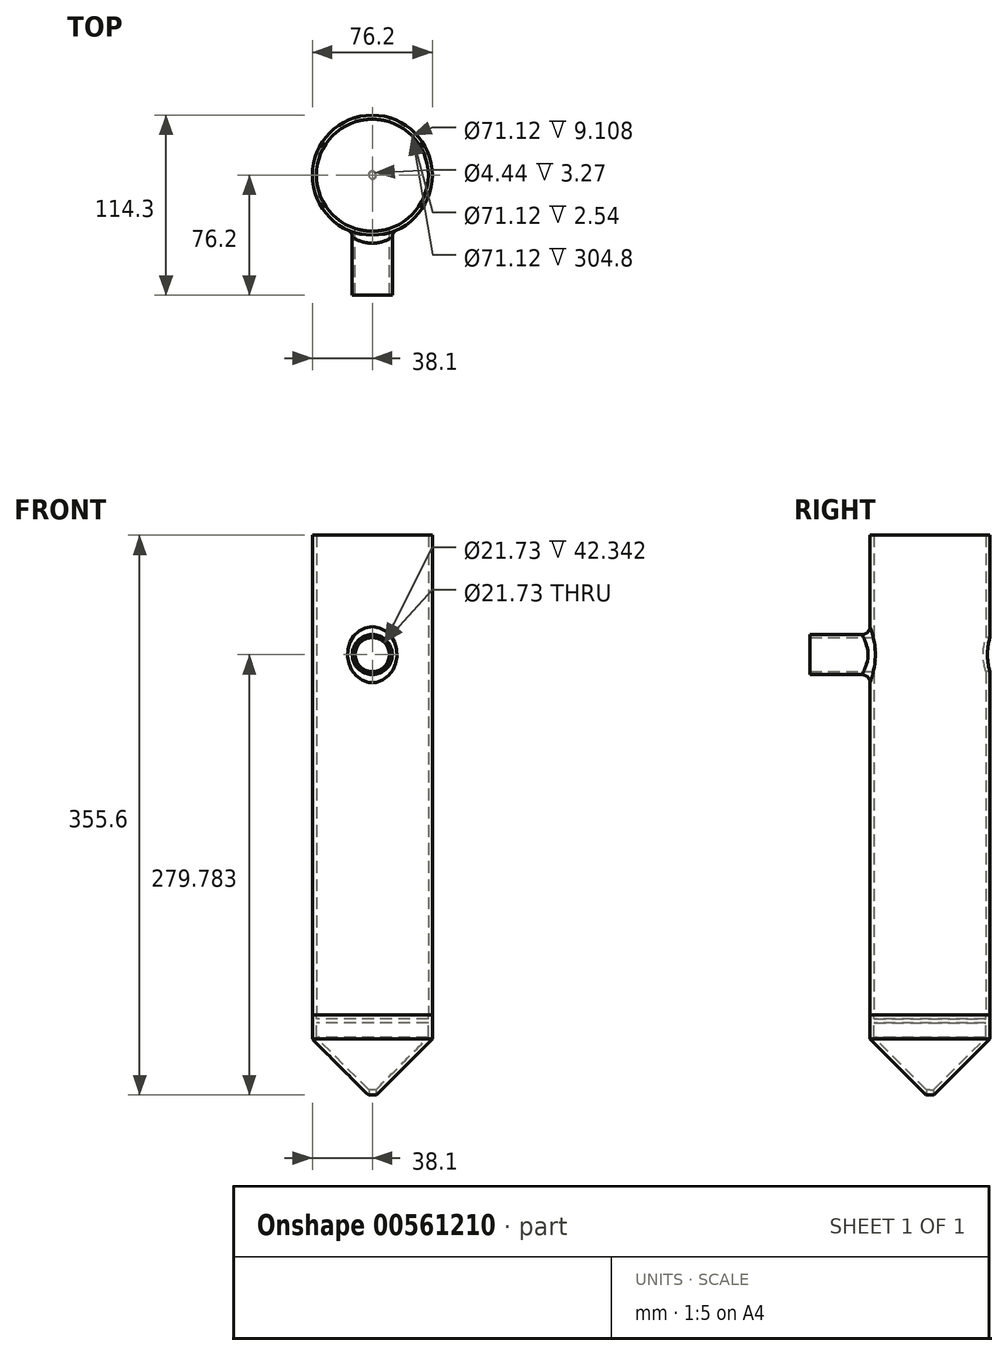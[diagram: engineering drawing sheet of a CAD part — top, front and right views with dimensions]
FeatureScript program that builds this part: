
annotation { "Feature Type Name" : "Feature", "Feature Type Description" : "" }
export const myFeature = defineFeature(function(context is Context, id is Id, definition is map)
    precondition{}
    {
        {
            var Q0;
            Q0=qCreatedBy(makeId("Top.planeOp"),FACE);
            var sketch = newSketch(context, id + "F0", { "sketchPlane" : qUnion([Q0])});
            skCircle(sketch, "E0", {"center": v(0, 0) * mm, "radius": 38.1 * mm});
            skSolve(sketch);
        }
        {
            var Q0;
            Q0 = qSketchRegion(id + "F0", true);
            extrude(context, id + "F1", {"entities" : qUnion([Q0]), "depth" : 304.8 * mm, "offsetDistance" : 25.4 * mm});
        }
        {
            var Q0;
            Q0=makeQuery(id+"F1.opExtrude","CAP_FACE",FACE,{"disambiguationData":[OSD([sQuery(id+"F0.wireOp",EDGE,"E0")])],"isStart":true});
            var sketch = newSketch(context, id + "F2", { "sketchPlane" : qUnion([Q0])});
            skCircle(sketch, "E1", {"center": v(0, 0) * mm, "radius": 38.1 * mm});
            skPoint(sketch, "E1.first.point", {"position": v(-6.24, 37.59) * mm});
            skPoint(sketch, "E1.second.point", {"position": v(37.6, -6.13) * mm});
            skPoint(sketch, "E1.third.point", {"position": v(-28.32, -25.5) * mm});
            skSolve(sketch);
        }
        {
            var Q0;
            Q0 = qSketchRegion(id + "F2", true);
            extrude(context, id + "F3", {"entities" : qUnion([Q0]), "depth" : 50.8 * mm, "offsetDistance" : 25.4 * mm});
        }
        {
            var Q0;
            Q0=makeQuery(id+"F3.opExtrude","CAP_EDGE",EDGE,{"disambiguationData":[OSD([sQuery(id+"F2.wireOp",EDGE,"E1")])],"isStart":false});
            chamfer(context, id + "F4", {"entities" : qUnion([Q0]), "width" : 35.56 * mm, "tangentPropagation" : true});
        }
        {
            var Q0;
            Q0=qCreatedBy(makeId("Front.planeOp"),FACE);
            var sketch = newSketch(context, id + "F5", { "sketchPlane" : qUnion([Q0])});
            skCircle(sketch, "E2", {"center": v(0, 228.98) * mm, "radius": 12.7 * mm});
            skCircle(sketch, "E3", {"center": v(0, 228.98) * mm, "radius": 10.87 * mm});
            skSolve(sketch);
        }
        {
            var Q0;
            Q0=makeQuery(id+"F1.opExtrude","CAP_FACE",FACE,{"disambiguationData":[OSD([sQuery(id+"F0.wireOp",EDGE,"E0")])],"isStart":false});
            shell(context, id + "F6", {"entities" : qUnion([Q0]), "thickness" : 2.54 * mm});
        }
        {
            var Q0;
            {var subQ0=sQuery(id+"F0.wireOp",EDGE,"E0");Q0=makeQuery(id+"F6.opShell","OFFSET_FACE",FACE,{"disambiguationData":[OSD([subQ0]),TDD([makeQuery(id+"F1.opExtrude","CAP_FACE",FACE,{"disambiguationData":[OSD([subQ0])],"isStart":true})])]});}
            var sketch = newSketch(context, id + "F7", { "sketchPlane" : qUnion([Q0])});
            skCircle(sketch, "E4", {"center": v(0, 0) * mm, "radius": 35.56 * mm});
            skPoint(sketch, "E4.first.point", {"position": v(-25.89, 24.38) * mm});
            skPoint(sketch, "E4.second.point", {"position": v(32.46, -14.53) * mm});
            skPoint(sketch, "E4.third.point", {"position": v(-23.4, -26.77) * mm});
            skSolve(sketch);
        }
        {
            var Q0;
            Q0 = qSketchRegion(id + "F7", true);
            extrude(context, id + "F8", {"entities" : qUnion([Q0]), "operationType" : NewBodyOperationType.REMOVE, "oppositeDirection" : true, "depth" : 5.08 * mm, "offsetDistance" : 25.4 * mm});
        }
        {
            var Q0;
            Q0=makeQuery(id+"F3.opExtrude","CAP_FACE",FACE,{"disambiguationData":[OSD([sQuery(id+"F2.wireOp",EDGE,"E1")])],"isStart":true});
            shell(context, id + "F9", {"entities" : qUnion([Q0]), "thickness" : 2.54 * mm});
        }
        {
            var Q0;
            Q0=makeQuery(id+"F3.opExtrude","CAP_FACE",FACE,{"disambiguationData":[OSD([sQuery(id+"F2.wireOp",EDGE,"E1")])],"isStart":false});
            var sketch = newSketch(context, id + "F10", { "sketchPlane" : qUnion([Q0])});
            skCircle(sketch, "E5", {"center": v(0, 0) * mm, "radius": 2.22 * mm});
            skSolve(sketch);
        }
        {
            var Q0;
            Q0 = qSketchRegion(id + "F10", true);
            extrude(context, id + "F11", {"entities" : qUnion([Q0]), "operationType" : NewBodyOperationType.REMOVE, "oppositeDirection" : true, "depth" : 25.4 * mm, "offsetDistance" : 25.4 * mm});
        }
        {
            var Q0;
            Q0 = qSketchRegion(id + "F5", true);
            extrude(context, id + "F12", {"entities" : qUnion([Q0]), "operationType" : NewBodyOperationType.ADD, "depth" : 76.2 * mm, "offsetDistance" : 25.4 * mm});
        }
        {
            var Q0;
            Q0=makeQuery(id+"F1.opExtrude","CAP_FACE",FACE,{"disambiguationData":[OSD([sQuery(id+"F0.wireOp",EDGE,"E0")])],"isStart":false});
            var sketch = newSketch(context, id + "F13", { "sketchPlane" : qUnion([Q0])});
            skCircle(sketch, "E6", {"center": v(0, 0) * mm, "radius": 35.56 * mm});
            skPoint(sketch, "E6.first.point", {"position": v(35.44, 2.86) * mm});
            skPoint(sketch, "E6.second.point", {"position": v(-28.12, -21.76) * mm});
            skPoint(sketch, "E6.third.point", {"position": v(-12.63, 33.24) * mm});
            skSolve(sketch);
        }
        {
            var Q0;
            Q0 = qSketchRegion(id + "F13", true);
            extrude(context, id + "F14", {"entities" : qUnion([Q0]), "operationType" : NewBodyOperationType.REMOVE, "oppositeDirection" : true, "depth" : 152.4 * mm, "offsetDistance" : 25.4 * mm});
        }
        {
            var Q0;
            Q0=makeQuery(id+"F12.opExtrude","CAP_FACE",FACE,{"disambiguationData":[OSD([sQuery(id+"F5.wireOp",EDGE,"E2"),sQuery(id+"F5.wireOp",EDGE,"E3")])],"isStart":false});
            var sketch = newSketch(context, id + "F15", { "sketchPlane" : qUnion([Q0])});
            skCircle(sketch, "E7", {"center": v(0, 228.98) * mm, "radius": 10.87 * mm});
            skPoint(sketch, "E7.first.point", {"position": v(10.8, 230.24) * mm});
            skPoint(sketch, "E7.second.point", {"position": v(-8.52, 222.24) * mm});
            skPoint(sketch, "E7.third.point", {"position": v(-4.06, 239.06) * mm});
            skSolve(sketch);
        }
        {
            var Q0;
            Q0 = qSketchRegion(id + "F15", true);
            extrude(context, id + "F16", {"entities" : qUnion([Q0]), "operationType" : NewBodyOperationType.REMOVE, "oppositeDirection" : true, "depth" : 127 * mm, "offsetDistance" : 25.4 * mm});
        }
        {
            var Q0;
            Q0=makeQuery(id+"F12.boolean.opBoolean","INTERSECT",EDGE,{"derivedFrom":[makeQuery(id+"F1.opExtrude","SWEPT_FACE",FACE,{"disambiguationData":[OSD([sQuery(id+"F0.wireOp",EDGE,"E0")])]}),makeQuery(id+"F12.opExtrude","SWEPT_FACE",FACE,{"disambiguationData":[OSD([sQuery(id+"F5.wireOp",EDGE,"E2")])]})]});
            fillet(context, id + "F17", {"entities" : qUnion([Q0]), "radius" : 5.08 * mm, "tangentPropagation" : true, "allowEdgeOverflow" : false});
        }
    });
